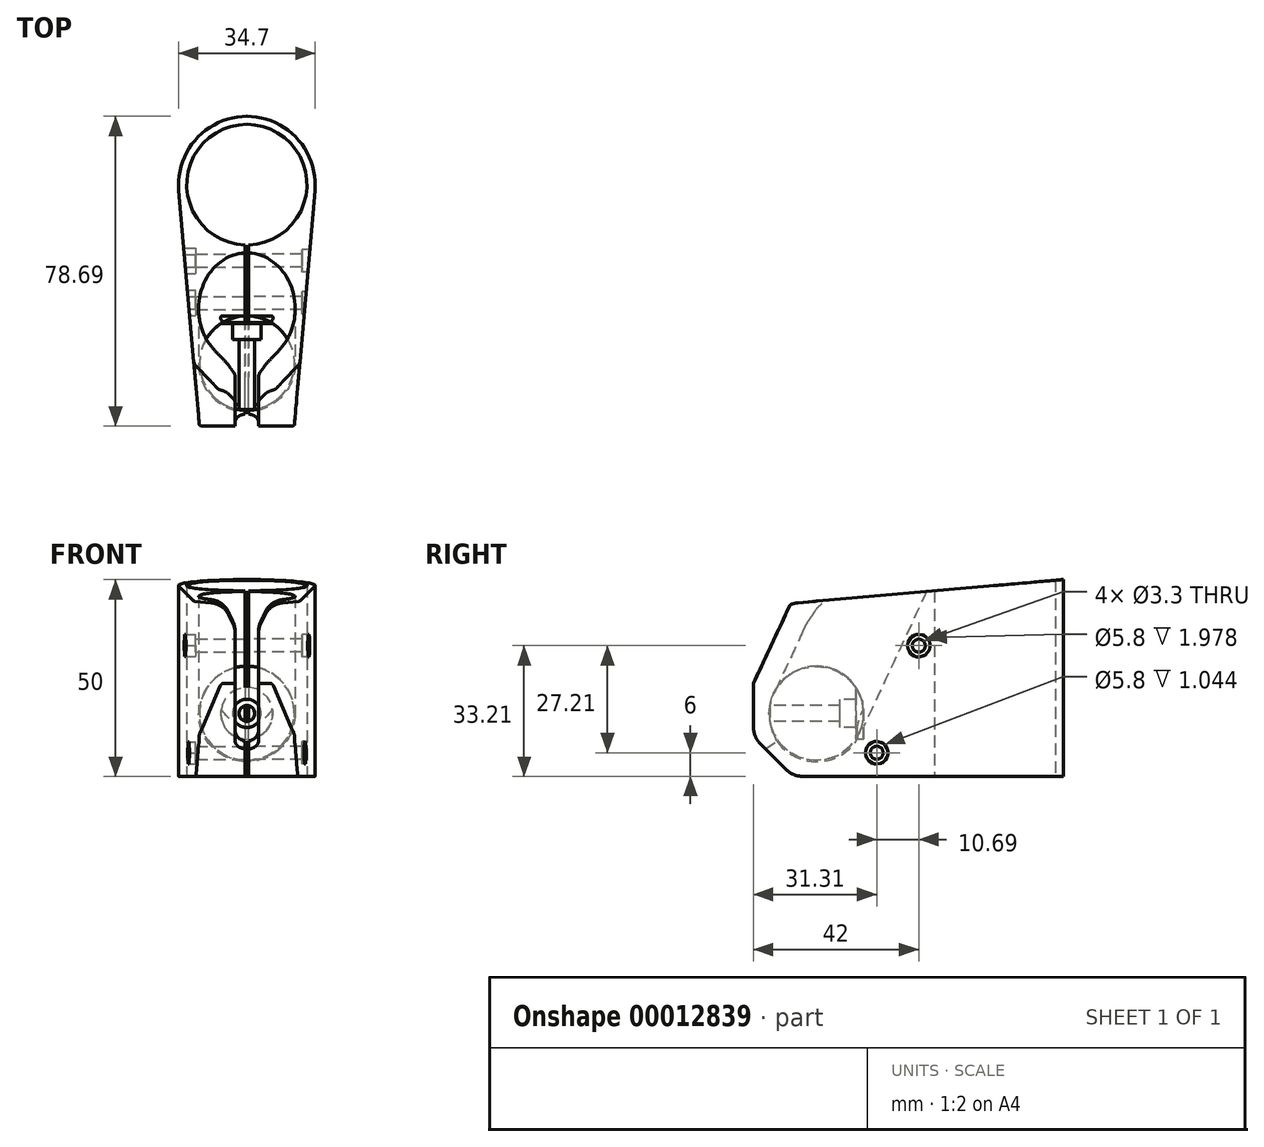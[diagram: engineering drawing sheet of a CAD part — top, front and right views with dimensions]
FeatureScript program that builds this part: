
annotation { "Feature Type Name" : "Feature", "Feature Type Description" : "" }
export const myFeature = defineFeature(function(context is Context, id is Id, definition is map)
    precondition{}
    {
        {
            var Q0;
            Q0=qCreatedBy(makeId("Top.planeOp"),FACE);
            var sketch = newSketch(context, id + "F0", { "sketchPlane" : qUnion([Q0])});
            skCircle(sketch, "E0", {"center": v(0, 0) * mm, "radius": 15.35 * mm, "construction": true});
            skSolve(sketch);
        }
        {
            var Q0;
            Q0=qCreatedBy(makeId("Top.planeOp"),FACE);
            var sketch = newSketch(context, id + "F1", { "sketchPlane" : qUnion([Q0])});
            skArc(sketch, "E1", {"start": v(0.5, -15.34) * mm, "mid": v(15.35, 0.25) * mm, "end": v(0, 15.35) * mm});
            skLineSegment(sketch, "E2", {"start": v(0.5, -15.34) * mm, "end": v(0.5, -61.34) * mm});
            skLineSegment(sketch, "E3", {"start": v(0.5, -61.34) * mm, "end": v(12.05, -61.34) * mm});
            skLineSegment(sketch, "E4", {"start": v(12.05, -61.34) * mm, "end": v(17.28, -1.51) * mm});
            skLineSegment(sketch, "E5", {"start": v(0, 0) * mm, "end": v(0, 15.35) * mm, "construction": true});
            skArc(sketch, "E6", {"start": v(17.28, -1.51) * mm, "mid": v(12.8, 11.72) * mm, "end": v(0, 17.35) * mm});
            skLineSegment(sketch, "E7", {"start": v(0, 15.35) * mm, "end": v(0, 17.35) * mm});
            skSolve(sketch);
        }
        {
            var Q0;
            Q0 = qSketchRegion(id + "F1", true);
            extrude(context, id + "F2", {"entities" : qUnion([Q0]), "depth" : 50 * mm});
        }
        {
            var Q0;
            Q0=qCreatedBy(makeId("Right.planeOp"),FACE);
            var sketch = newSketch(context, id + "F3", { "sketchPlane" : qUnion([Q0])});
            skLineSegment(sketch, "E8", {"start": v(-22.2, 65.65) * mm, "end": v(-50.54, 4.85) * mm});
            skArc(sketch, "E9", {"start": v(-56.49, 21.2) * mm, "mid": v(-56.9, 11.8) * mm, "end": v(-50.54, 4.85) * mm});
            skLineSegment(sketch, "E10", {"start": v(-56.49, 21.2) * mm, "end": v(-33.34, 70.84) * mm});
            skLineSegment(sketch, "E11", {"start": v(-33.34, 70.84) * mm, "end": v(-22.2, 65.65) * mm});
            skSolve(sketch);
        }
        {
            var Q0;
            Q0 = qSketchRegion(id + "F3", true);
            var Q1;
            Q1=sQuery(id+"F3.wireOp",EDGE,"E8");
            revolve(context, id + "F4", {"operationType" : NewBodyOperationType.REMOVE, "entities" : qUnion([Q0]), "axis" : qUnion([Q1]), "revolveType" : RevolveType.FULL});
        }
        {
            var Q0;
            Q0=makeQuery(id+"F2.opExtrude","CAP_EDGE",EDGE,{"disambiguationData":[OSD([sQuery(id+"F1.wireOp",EDGE,"E3")])],"isStart":true});
            chamfer(context, id + "F5", {"entities" : qUnion([Q0]), "width" : 10 * mm, "tangentPropagation" : true});
        }
        {
            var Q0;
            Q0=qCreatedBy(makeId("Right.planeOp"),FACE);
            var sketch = newSketch(context, id + "F6", { "sketchPlane" : qUnion([Q0])});
            skCircle(sketch, "E12", {"center": v(-19.34, 33.21) * mm, "radius": 1.65 * mm});
            skCircle(sketch, "E13", {"center": v(-30.03, 6) * mm, "radius": 1.65 * mm});
            skLineSegment(sketch, "E14", {"start": v(-30.03, 6) * mm, "end": v(-19.34, 33.21) * mm, "construction": true});
            skLineSegment(sketch, "E15", {"start": v(-30.03, 6) * mm, "end": v(-30.03, 0) * mm, "construction": true});
            skLineSegment(sketch, "E16", {"start": v(-30.03, 6) * mm, "end": v(-35.05, 9.28) * mm, "construction": true});
            skLineSegment(sketch, "E17", {"start": v(-19.34, 33.21) * mm, "end": v(-22.97, 34.9) * mm, "construction": true});
            skLineSegment(sketch, "E18", {"start": v(-19.34, 33.21) * mm, "end": v(-15.34, 33.21) * mm, "construction": true});
            skLineSegment(sketch, "E19", {"start": v(-35.05, 9.28) * mm, "end": v(-31.35, 14.95) * mm, "construction": true});
            skSolve(sketch);
        }
        {
            var Q0;
            Q0 = qSketchRegion(id + "F6", true);
            extrude(context, id + "F7", {"entities" : qUnion([Q0]), "operationType" : NewBodyOperationType.REMOVE, "endBound" : BoundingType.THROUGH_ALL, "depth" : 25 * mm});
        }
        {
            var Q0;
            Q0=qCreatedBy(makeId("Right.planeOp"),FACE);
            var sketch = newSketch(context, id + "F8", { "sketchPlane" : qUnion([Q0])});
            skLineSegment(sketch, "E20", {"start": v(-61.34, 50) * mm, "end": v(-49.05, 50) * mm});
            skLineSegment(sketch, "E21", {"start": v(-49.05, 50) * mm, "end": v(-61.34, 23.64) * mm});
            skLineSegment(sketch, "E22", {"start": v(-61.34, 23.64) * mm, "end": v(-61.34, 50) * mm});
            skLineSegment(sketch, "E23", {"start": v(-43.05, 50) * mm, "end": v(-49.05, 50) * mm, "construction": true});
            skSolve(sketch);
        }
        {
            var Q0;
            Q0 = qSketchRegion(id + "F8", true);
            extrude(context, id + "F9", {"entities" : qUnion([Q0]), "operationType" : NewBodyOperationType.REMOVE, "endBound" : BoundingType.THROUGH_ALL, "depth" : 25 * mm});
        }
        {
            var Q0;
            Q0=qCreatedBy(makeId("Right.planeOp"),FACE);
            var sketch = newSketch(context, id + "F10", { "sketchPlane" : qUnion([Q0])});
            skLineSegment(sketch, "E24", {"start": v(-29.49, 50) * mm, "end": v(-45.34, 16) * mm});
            skLineSegment(sketch, "E25", {"start": v(-45.34, 16) * mm, "end": v(-74.39, -4.34) * mm});
            skLineSegment(sketch, "E26", {"start": v(-74.39, -4.34) * mm, "end": v(-49.05, 50) * mm});
            skLineSegment(sketch, "E27", {"start": v(-49.05, 50) * mm, "end": v(-29.49, 50) * mm});
            skSolve(sketch);
        }
        {
            var Q0;
            Q0 = qSketchRegion(id + "F10", true);
            extrude(context, id + "F11", {"entities" : qUnion([Q0]), "operationType" : NewBodyOperationType.REMOVE, "endBound" : BoundingType.SYMMETRIC, "depth" : 6 * mm});
        }
        {
            var Q0;
            Q0=makeQuery(id+"F11.boolean.opBoolean","COPY",EDGE,{"derivedFrom":makeQuery(id+"F11.opExtrude","CAP_EDGE",EDGE,{"disambiguationData":[OSD([sQuery(id+"F10.wireOp",EDGE,"E25")])],"isStart":false})});
            fillet(context, id + "F12", {"entities" : qUnion([Q0]), "radius" : 3 * mm, "tangentPropagation" : true, "allowEdgeOverflow" : false});
        }
        {
            var Q0;
            Q0=makeQuery(id+"F9.boolean.opBoolean","COPY",EDGE,{"derivedFrom":makeQuery(id+"F9.opExtrude","SWEPT_EDGE",EDGE,{"disambiguationData":[OSD([sQuery(id+"F8.wireOp",EDGE,"E21"),sQuery(id+"F8.wireOp",EDGE,"E22")])]})});
            var Q1;
            {var subQ0=sQuery(id+"F1.wireOp",EDGE,"E3");Q1=makeQuery(id+"F5.opChamfer","BLEND_EDGE",EDGE,{"blendedFrom":[makeQuery(id+"F2.opExtrude","CAP_EDGE",EDGE,{"disambiguationData":[OSD([subQ0])],"isStart":true}),makeQuery(id+"F2.opExtrude","SWEPT_FACE",FACE,{"disambiguationData":[OSD([subQ0])]})],"blendedInto":[makeQuery(id+"F2.opExtrude","SWEPT_FACE",FACE,{"disambiguationData":[OSD([subQ0])]})]});}
            var Q2;
            {var subQ0=sQuery(id+"F1.wireOp",EDGE,"E3");Q2=makeQuery(id+"F5.opChamfer","BLEND_EDGE",EDGE,{"blendedFrom":[makeQuery(id+"F2.opExtrude","CAP_EDGE",EDGE,{"disambiguationData":[OSD([subQ0])],"isStart":true}),makeQuery(id+"F2.opExtrude","CAP_FACE",FACE,{"disambiguationData":[OSD([sQuery(id+"F1.wireOp",EDGE,"E1"),sQuery(id+"F1.wireOp",EDGE,"E2"),subQ0,sQuery(id+"F1.wireOp",EDGE,"E4"),sQuery(id+"F1.wireOp",EDGE,"E6"),sQuery(id+"F1.wireOp",EDGE,"E7")])],"isStart":true})],"blendedInto":[makeQuery(id+"F2.opExtrude","CAP_FACE",FACE,{"disambiguationData":[OSD([sQuery(id+"F1.wireOp",EDGE,"E1"),sQuery(id+"F1.wireOp",EDGE,"E2"),subQ0,sQuery(id+"F1.wireOp",EDGE,"E4"),sQuery(id+"F1.wireOp",EDGE,"E6"),sQuery(id+"F1.wireOp",EDGE,"E7")])],"isStart":true})]});}
            fillet(context, id + "F13", {"entities" : qUnion([Q0, Q1, Q2]), "radius" : 6 * mm, "tangentPropagation" : true, "allowEdgeOverflow" : false});
        }
        {
            var Q0;
            Q0=makeQuery(id+"F2.opExtrude","SWEPT_BODY",BODY,{"disambiguationData":[OSD([sQuery(id+"F1.wireOp",EDGE,"E1"),sQuery(id+"F1.wireOp",EDGE,"E2"),sQuery(id+"F1.wireOp",EDGE,"E3"),sQuery(id+"F1.wireOp",EDGE,"E4"),sQuery(id+"F1.wireOp",EDGE,"E6"),sQuery(id+"F1.wireOp",EDGE,"E7")])]});
            var Q1;
            Q1=makeQuery(id+"F2.opExtrude","SWEPT_FACE",FACE,{"disambiguationData":[OSD([sQuery(id+"F1.wireOp",EDGE,"E7")])]});
            mirror(context, id + "F14", {"operationType" : NewBodyOperationType.ADD, "entities" : qUnion([Q0]), "mirrorPlane" : qUnion([Q1])});
        }
        {
            var Q0;
            Q0=makeQuery(id+"F14.opPattern","COPY",EDGE,{"derivedFrom":makeQuery(id+"F9.boolean.opBoolean","INTERSECT",EDGE,{"derivedFrom":[makeQuery(id+"F2.opExtrude","SWEPT_FACE",FACE,{"disambiguationData":[OSD([sQuery(id+"F1.wireOp",EDGE,"E4")])]}),makeQuery(id+"F9.opExtrude","SWEPT_FACE",FACE,{"disambiguationData":[OSD([sQuery(id+"F8.wireOp",EDGE,"E21")])]})]}),"instanceName":"1"});
            var Q1;
            Q1=makeQuery(id+"F9.boolean.opBoolean","INTERSECT",EDGE,{"derivedFrom":[makeQuery(id+"F2.opExtrude","SWEPT_FACE",FACE,{"disambiguationData":[OSD([sQuery(id+"F1.wireOp",EDGE,"E4")])]}),makeQuery(id+"F9.opExtrude","SWEPT_FACE",FACE,{"disambiguationData":[OSD([sQuery(id+"F8.wireOp",EDGE,"E21")])]})]});
            chamfer(context, id + "F15", {"entities" : qUnion([Q0, Q1]), "width" : 6 * mm});
        }
        {
            var Q0;
            Q0=qCreatedBy(makeId("Right.planeOp"),FACE);
            var sketch = newSketch(context, id + "F16", { "sketchPlane" : qUnion([Q0])});
            skLineSegment(sketch, "E28", {"start": v(-34.47, 10.93) * mm, "end": v(-56.22, 21.07) * mm});
            skArc(sketch, "E29", {"start": v(-56.22, 21.07) * mm, "mid": v(-50.41, 5.12) * mm, "end": v(-34.47, 10.93) * mm});
            skSolve(sketch);
        }
        {
            var Q0;
            Q0 = qSketchRegion(id + "F16", true);
            var Q1;
            Q1=sQuery(id+"F16.wireOp",EDGE,"E28");
            revolve(context, id + "F17", {"entities" : qUnion([Q0]), "axis" : qUnion([Q1]), "revolveType" : RevolveType.FULL});
        }
        {
            var Q0;
            {var subQ0=makeQuery(id+"F2.opExtrude","CAP_EDGE",EDGE,{"disambiguationData":[OSD([sQuery(id+"F1.wireOp",EDGE,"E6")])],"isStart":true});Q0=makeQuery(id+"F14.boolean.opBoolean","MERGE",EDGE,{"derivedFrom":[subQ0,makeQuery(id+"F14.opPattern","COPY",EDGE,{"derivedFrom":subQ0,"instanceName":"1"})]});}
            var Q1;
            {var subQ0=makeQuery(id+"F2.opExtrude","SWEPT_FACE",FACE,{"disambiguationData":[OSD([sQuery(id+"F1.wireOp",EDGE,"E4")])]});Q1=makeQuery(id+"F15.opChamfer","BLEND_EDGE",EDGE,{"blendedFrom":[makeQuery(id+"F14.opPattern","COPY",EDGE,{"derivedFrom":makeQuery(id+"F9.boolean.opBoolean","INTERSECT",EDGE,{"derivedFrom":[subQ0,makeQuery(id+"F9.opExtrude","SWEPT_FACE",FACE,{"disambiguationData":[OSD([sQuery(id+"F8.wireOp",EDGE,"E21")])]})]}),"instanceName":"1"}),makeQuery(id+"F14.opPattern","COPY",FACE,{"derivedFrom":subQ0,"instanceName":"1"})],"blendedInto":[makeQuery(id+"F14.opPattern","COPY",FACE,{"derivedFrom":subQ0,"instanceName":"1"})]});}
            var Q2;
            {var subQ0=makeQuery(id+"F9.opExtrude","SWEPT_FACE",FACE,{"disambiguationData":[OSD([sQuery(id+"F8.wireOp",EDGE,"E21")])]});Q2=makeQuery(id+"F15.opChamfer","BLEND_EDGE",EDGE,{"blendedFrom":[makeQuery(id+"F14.opPattern","COPY",EDGE,{"derivedFrom":makeQuery(id+"F9.boolean.opBoolean","INTERSECT",EDGE,{"derivedFrom":[makeQuery(id+"F2.opExtrude","SWEPT_FACE",FACE,{"disambiguationData":[OSD([sQuery(id+"F1.wireOp",EDGE,"E4")])]}),subQ0]}),"instanceName":"1"}),makeQuery(id+"F14.opPattern","COPY",FACE,{"derivedFrom":makeQuery(id+"F9.boolean.opBoolean","COPY",FACE,{"derivedFrom":subQ0}),"instanceName":"1"})],"blendedInto":[makeQuery(id+"F14.opPattern","COPY",FACE,{"derivedFrom":makeQuery(id+"F9.boolean.opBoolean","COPY",FACE,{"derivedFrom":subQ0}),"instanceName":"1"})]});}
            var Q3;
            {var subQ0=makeQuery(id+"F9.opExtrude","SWEPT_FACE",FACE,{"disambiguationData":[OSD([sQuery(id+"F8.wireOp",EDGE,"E21")])]});Q3=makeQuery(id+"F15.opChamfer","BLEND_EDGE",EDGE,{"blendedFrom":[makeQuery(id+"F9.boolean.opBoolean","INTERSECT",EDGE,{"derivedFrom":[makeQuery(id+"F2.opExtrude","SWEPT_FACE",FACE,{"disambiguationData":[OSD([sQuery(id+"F1.wireOp",EDGE,"E4")])]}),subQ0]}),makeQuery(id+"F9.boolean.opBoolean","COPY",FACE,{"derivedFrom":subQ0})],"blendedInto":[makeQuery(id+"F9.boolean.opBoolean","COPY",FACE,{"derivedFrom":subQ0})]});}
            var Q4;
            {var subQ0=makeQuery(id+"F2.opExtrude","SWEPT_FACE",FACE,{"disambiguationData":[OSD([sQuery(id+"F1.wireOp",EDGE,"E4")])]});Q4=makeQuery(id+"F15.opChamfer","BLEND_EDGE",EDGE,{"blendedFrom":[makeQuery(id+"F9.boolean.opBoolean","INTERSECT",EDGE,{"derivedFrom":[subQ0,makeQuery(id+"F9.opExtrude","SWEPT_FACE",FACE,{"disambiguationData":[OSD([sQuery(id+"F8.wireOp",EDGE,"E21")])]})]}),subQ0],"blendedInto":[subQ0]});}
            fillet(context, id + "F18", {"entities" : qUnion([Q0, Q1, Q2, Q3, Q4]), "radius" : 1 * mm, "tangentPropagation" : true, "rho" : .2, "crossSection" : FilletCrossSection.CONIC, "allowEdgeOverflow" : false});
        }
        {
            var Q0;
            Q0=qCreatedBy(makeId("Right.planeOp"),FACE);
            var sketch = newSketch(context, id + "F19", { "sketchPlane" : qUnion([Q0])});
            skLineSegment(sketch, "E30", {"start": v(-33.34, 16) * mm, "end": v(-57.34, 16) * mm});
            skLineSegment(sketch, "E31", {"start": v(-57.34, 16) * mm, "end": v(-57.34, 18) * mm});
            skLineSegment(sketch, "E32", {"start": v(-57.34, 18) * mm, "end": v(-39.34, 18) * mm});
            skLineSegment(sketch, "E33", {"start": v(-39.34, 18) * mm, "end": v(-39.34, 19.6) * mm});
            skLineSegment(sketch, "E34", {"start": v(-33.34, 19.6) * mm, "end": v(-33.34, 16) * mm});
            skCircle(sketch, "E35", {"center": v(-45.34, 16) * mm, "radius": 12 * mm, "construction": true});
            skLineSegment(sketch, "E36", {"start": v(-39.34, 19.6) * mm, "end": v(-35.34, 19.6) * mm});
            skLineSegment(sketch, "E37", {"start": v(-35.34, 19.6) * mm, "end": v(-35.34, 22.63) * mm});
            skLineSegment(sketch, "E38", {"start": v(-35.34, 22.63) * mm, "end": v(-33.34, 22.63) * mm});
            skLineSegment(sketch, "E39", {"start": v(-33.34, 22.63) * mm, "end": v(-33.34, 19.6) * mm});
            skSolve(sketch);
        }
        {
            var Q0;
            Q0 = qSketchRegion(id + "F19", true);
            var Q1;
            Q1=sQuery(id+"F19.wireOp",EDGE,"E30");
            revolve(context, id + "F20", {"operationType" : NewBodyOperationType.REMOVE, "entities" : qUnion([Q0]), "axis" : qUnion([Q1]), "revolveType" : RevolveType.FULL, "oppositeDirection" : true});
        }
        {
            var Q0;
            Q0=qCreatedBy(makeId("Right.planeOp"),FACE);
            var sketch = newSketch(context, id + "F21", { "sketchPlane" : qUnion([Q0])});
            skLineSegment(sketch, "E40", {"start": v(17.35, 50) * mm, "end": v(-84.6, 50) * mm});
            skLineSegment(sketch, "E41", {"start": v(-84.6, 50) * mm, "end": v(-84.6, 41.08) * mm});
            skLineSegment(sketch, "E42", {"start": v(-84.6, 41.08) * mm, "end": v(17.35, 50) * mm});
            skSolve(sketch);
        }
        {
            var Q0;
            Q0 = qSketchRegion(id + "F21", true);
            extrude(context, id + "F22", {"entities" : qUnion([Q0]), "operationType" : NewBodyOperationType.REMOVE, "endBound" : BoundingType.THROUGH_ALL, "oppositeDirection" : true, "depth" : 25 * mm, "hasSecondDirection" : true, "secondDirectionBound" : SecondDirectionBoundingType.THROUGH_ALL, "secondDirectionOppositeDirection" : false, "secondDirectionDepth" : 25 * mm});
        }
        {
            var Q0;
            Q0=makeQuery(id+"F22.boolean.opBoolean","INTERSECT",EDGE,{"derivedFrom":[makeQuery(id+"F11.boolean.opBoolean","COPY",FACE,{"derivedFrom":makeQuery(id+"F11.opExtrude","CAP_FACE",FACE,{"disambiguationData":[OSD([sQuery(id+"F10.wireOp",EDGE,"E24"),sQuery(id+"F10.wireOp",EDGE,"E25"),sQuery(id+"F10.wireOp",EDGE,"E26"),sQuery(id+"F10.wireOp",EDGE,"E27")])],"isStart":false})}),makeQuery(id+"F22.opExtrude","SWEPT_FACE",FACE,{"disambiguationData":[OSD([sQuery(id+"F21.wireOp",EDGE,"E42")])]})]});
            var Q1;
            Q1=makeQuery(id+"F22.boolean.opBoolean","INTERSECT",EDGE,{"derivedFrom":[makeQuery(id+"F14.opPattern","COPY",FACE,{"derivedFrom":makeQuery(id+"F11.boolean.opBoolean","COPY",FACE,{"derivedFrom":makeQuery(id+"F11.opExtrude","CAP_FACE",FACE,{"disambiguationData":[OSD([sQuery(id+"F10.wireOp",EDGE,"E24"),sQuery(id+"F10.wireOp",EDGE,"E25"),sQuery(id+"F10.wireOp",EDGE,"E26"),sQuery(id+"F10.wireOp",EDGE,"E27")])],"isStart":false})}),"instanceName":"1"}),makeQuery(id+"F22.opExtrude","SWEPT_FACE",FACE,{"disambiguationData":[OSD([sQuery(id+"F21.wireOp",EDGE,"E42")])]})]});
            chamfer(context, id + "F23", {"entities" : qUnion([Q0, Q1]), "chamferType" : ChamferType.TWO_OFFSETS, "width1" : 6 * mm, "oppositeDirection" : false, "width2" : 3 * mm, "tangentPropagation" : true});
        }
        {
            var Q0;
            {var subQ0=makeQuery(id+"F22.opExtrude","SWEPT_FACE",FACE,{"disambiguationData":[OSD([sQuery(id+"F21.wireOp",EDGE,"E42")])]});Q0=makeQuery(id+"F23.opChamfer","BLEND_EDGE",EDGE,{"blendedFrom":[makeQuery(id+"F22.boolean.opBoolean","INTERSECT",EDGE,{"derivedFrom":[makeQuery(id+"F11.boolean.opBoolean","COPY",FACE,{"derivedFrom":makeQuery(id+"F11.opExtrude","CAP_FACE",FACE,{"disambiguationData":[OSD([sQuery(id+"F10.wireOp",EDGE,"E24"),sQuery(id+"F10.wireOp",EDGE,"E25"),sQuery(id+"F10.wireOp",EDGE,"E26"),sQuery(id+"F10.wireOp",EDGE,"E27")])],"isStart":false})}),subQ0]}),makeQuery(id+"F22.boolean.opBoolean","COPY",FACE,{"derivedFrom":subQ0})],"blendedInto":[makeQuery(id+"F22.boolean.opBoolean","COPY",FACE,{"derivedFrom":subQ0})]});}
            var Q1;
            {var subQ0=makeQuery(id+"F22.opExtrude","SWEPT_FACE",FACE,{"disambiguationData":[OSD([sQuery(id+"F21.wireOp",EDGE,"E42")])]});Q1=makeQuery(id+"F23.opChamfer","BLEND_EDGE",EDGE,{"blendedFrom":[makeQuery(id+"F22.boolean.opBoolean","INTERSECT",EDGE,{"derivedFrom":[makeQuery(id+"F14.opPattern","COPY",FACE,{"derivedFrom":makeQuery(id+"F11.boolean.opBoolean","COPY",FACE,{"derivedFrom":makeQuery(id+"F11.opExtrude","CAP_FACE",FACE,{"disambiguationData":[OSD([sQuery(id+"F10.wireOp",EDGE,"E24"),sQuery(id+"F10.wireOp",EDGE,"E25"),sQuery(id+"F10.wireOp",EDGE,"E26"),sQuery(id+"F10.wireOp",EDGE,"E27")])],"isStart":false})}),"instanceName":"1"}),subQ0]}),makeQuery(id+"F22.boolean.opBoolean","COPY",FACE,{"derivedFrom":subQ0})],"blendedInto":[makeQuery(id+"F22.boolean.opBoolean","COPY",FACE,{"derivedFrom":subQ0})]});}
            var Q2;
            {var subQ0=makeQuery(id+"F11.boolean.opBoolean","COPY",FACE,{"derivedFrom":makeQuery(id+"F11.opExtrude","CAP_FACE",FACE,{"disambiguationData":[OSD([sQuery(id+"F10.wireOp",EDGE,"E24"),sQuery(id+"F10.wireOp",EDGE,"E25"),sQuery(id+"F10.wireOp",EDGE,"E26"),sQuery(id+"F10.wireOp",EDGE,"E27")])],"isStart":false})});Q2=makeQuery(id+"F23.opChamfer","BLEND_EDGE",EDGE,{"blendedFrom":[makeQuery(id+"F22.boolean.opBoolean","INTERSECT",EDGE,{"derivedFrom":[subQ0,makeQuery(id+"F22.opExtrude","SWEPT_FACE",FACE,{"disambiguationData":[OSD([sQuery(id+"F21.wireOp",EDGE,"E42")])]})]}),subQ0],"blendedInto":[subQ0]});}
            var Q3;
            {var subQ0=makeQuery(id+"F14.opPattern","COPY",FACE,{"derivedFrom":makeQuery(id+"F11.boolean.opBoolean","COPY",FACE,{"derivedFrom":makeQuery(id+"F11.opExtrude","CAP_FACE",FACE,{"disambiguationData":[OSD([sQuery(id+"F10.wireOp",EDGE,"E24"),sQuery(id+"F10.wireOp",EDGE,"E25"),sQuery(id+"F10.wireOp",EDGE,"E26"),sQuery(id+"F10.wireOp",EDGE,"E27")])],"isStart":false})}),"instanceName":"1"});Q3=makeQuery(id+"F23.opChamfer","BLEND_EDGE",EDGE,{"blendedFrom":[makeQuery(id+"F22.boolean.opBoolean","INTERSECT",EDGE,{"derivedFrom":[subQ0,makeQuery(id+"F22.opExtrude","SWEPT_FACE",FACE,{"disambiguationData":[OSD([sQuery(id+"F21.wireOp",EDGE,"E42")])]})]}),subQ0],"blendedInto":[subQ0]});}
            fillet(context, id + "F24", {"entities" : qUnion([Q0, Q1, Q2, Q3]), "radius" : 5 * mm, "tangentPropagation" : true, "allowEdgeOverflow" : false});
        }
        {
            var Q0;
            Q0=qCreatedBy(makeId("Right.planeOp"),FACE);
            cPlane(context, id + "F25", {"entities" : qUnion([Q0]), "cplaneType" : CPlaneType.OFFSET, "offset" : 14 * mm, "width" : 150 * mm, "height" : 150 * mm});
        }
        {
            var Q0;
            Q0=qCreatedBy(makeId("Right.planeOp"),FACE);
            cPlane(context, id + "F26", {"entities" : qUnion([Q0]), "cplaneType" : CPlaneType.OFFSET, "offset" : 13 * mm, "oppositeDirection" : true, "width" : 150 * mm, "height" : 150 * mm});
        }
        {
            var Q0;
            Q0=qCreatedBy(id+"F25.planeOp",FACE);
            var sketch = newSketch(context, id + "F27", { "sketchPlane" : qUnion([Q0])});
            skCircle(sketch, "E43", {"center": v(-19.34, 33.21) * mm, "radius": 2.9 * mm});
            skCircle(sketch, "E44", {"center": v(-30.03, 6) * mm, "radius": 2.9 * mm});
            skSolve(sketch);
        }
        {
            var Q0;
            Q0 = qSketchRegion(id + "F27", true);
            extrude(context, id + "F28", {"entities" : qUnion([Q0]), "operationType" : NewBodyOperationType.REMOVE, "endBound" : BoundingType.THROUGH_ALL, "depth" : 25 * mm});
        }
        {
            var Q0;
            Q0=qCreatedBy(id+"F26.planeOp",FACE);
            var sketch = newSketch(context, id + "F29", { "sketchPlane" : qUnion([Q0])});
            skCircle(sketch, "E45", {"center": v(-19.34, 33.21) * mm, "radius": 3.23 * mm, "construction": true});
            skLineSegment(sketch, "E46", {"start": v(-17.73, 36.01) * mm, "end": v(-20.96, 36.01) * mm});
            skLineSegment(sketch, "E47", {"start": v(-20.96, 36.01) * mm, "end": v(-22.58, 33.21) * mm});
            skLineSegment(sketch, "E48", {"start": v(-22.58, 33.21) * mm, "end": v(-20.96, 30.41) * mm});
            skLineSegment(sketch, "E49", {"start": v(-20.96, 30.41) * mm, "end": v(-17.73, 30.41) * mm});
            skLineSegment(sketch, "E50", {"start": v(-17.73, 30.41) * mm, "end": v(-16.1, 33.21) * mm});
            skLineSegment(sketch, "E51", {"start": v(-16.1, 33.21) * mm, "end": v(-17.73, 36.01) * mm});
            skLineSegment(sketch, "E52", {"start": v(-31.64, 3.2) * mm, "end": v(-28.41, 3.2) * mm});
            skLineSegment(sketch, "E53", {"start": v(-26.8, 6) * mm, "end": v(-28.41, 8.8) * mm});
            skLineSegment(sketch, "E54", {"start": v(-33.26, 6) * mm, "end": v(-31.64, 3.2) * mm});
            skLineSegment(sketch, "E55", {"start": v(-28.41, 3.2) * mm, "end": v(-26.8, 6) * mm});
            skLineSegment(sketch, "E56", {"start": v(-31.64, 8.8) * mm, "end": v(-33.26, 6) * mm});
            skCircle(sketch, "E57", {"center": v(-30.03, 6) * mm, "radius": 3.23 * mm, "construction": true});
            skLineSegment(sketch, "E58", {"start": v(-28.41, 8.8) * mm, "end": v(-31.64, 8.8) * mm});
            skSolve(sketch);
        }
        {
            var Q0;
            Q0 = qSketchRegion(id + "F29", true);
            extrude(context, id + "F30", {"entities" : qUnion([Q0]), "operationType" : NewBodyOperationType.REMOVE, "endBound" : BoundingType.THROUGH_ALL, "oppositeDirection" : true, "depth" : 25 * mm});
        }
    });
